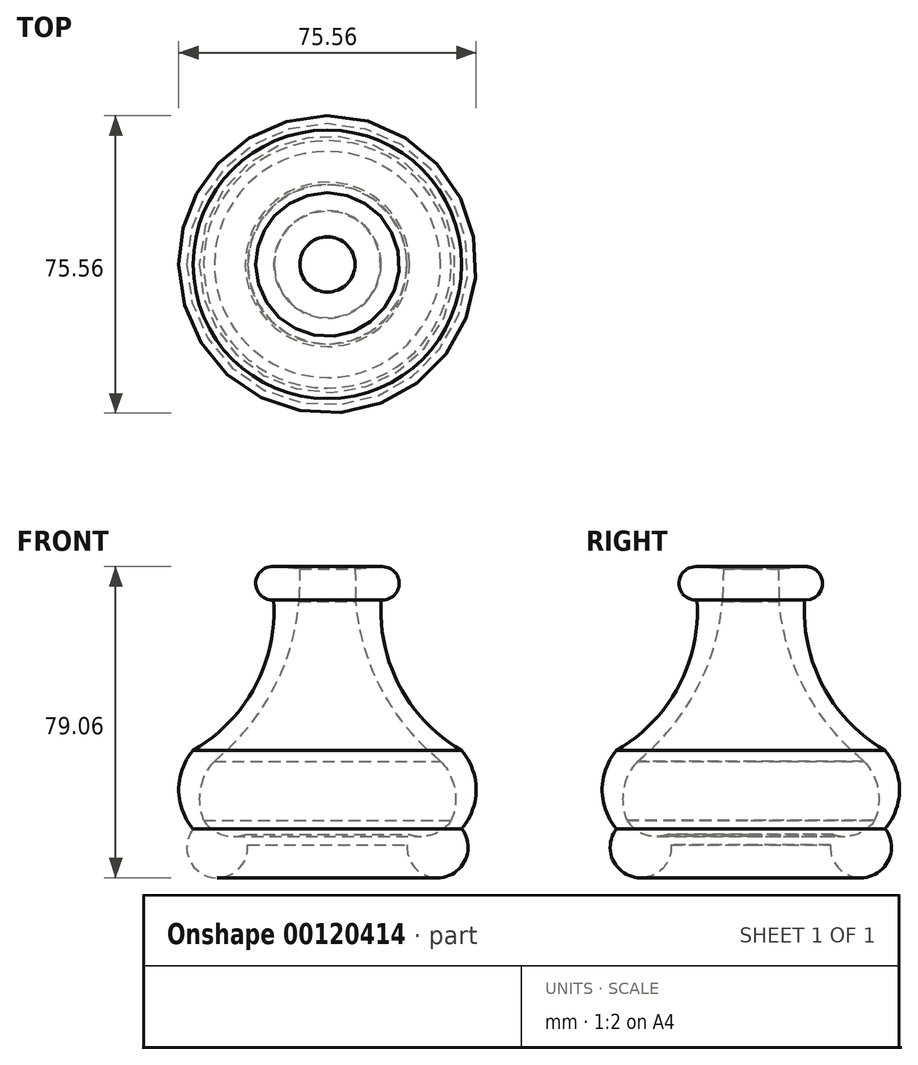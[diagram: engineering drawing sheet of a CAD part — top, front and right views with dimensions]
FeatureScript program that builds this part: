
annotation { "Feature Type Name" : "Feature", "Feature Type Description" : "" }
export const myFeature = defineFeature(function(context is Context, id is Id, definition is map)
    precondition{}
    {
        {
            var Q0;
            Q0=qCreatedBy(makeId("Front.planeOp"),FACE);
            var sketch = newSketch(context, id + "F0", { "sketchPlane" : qUnion([Q0])});
            skLineSegment(sketch, "E0", {"start": v(0, 0) * mm, "end": v(20.26, 0) * mm});
            skArc(sketch, "E1", {"start": v(20.26, 0) * mm, "mid": v(30.2, -8.02) * mm, "end": v(34.11, 4.13) * mm});
            skArc(sketch, "E2", {"start": v(34.11, 4.13) * mm, "mid": v(37.78, 14.06) * mm, "end": v(34.11, 23.98) * mm});
            skArc(sketch, "E3", {"start": v(13.65, 62.23) * mm, "mid": v(18.44, 40.2) * mm, "end": v(34.11, 23.98) * mm});
            skLineSegment(sketch, "E4", {"start": v(13.65, 70.7) * mm, "end": v(7, 70.18) * mm});
            skArc(sketch, "E5", {"start": v(7.22, 61.85) * mm, "mid": v(13.85, 39.38) * mm, "end": v(28.74, 21.29) * mm});
            skArc(sketch, "E6", {"start": v(31.43, 6.2) * mm, "mid": v(32.33, 14.14) * mm, "end": v(28.74, 21.29) * mm});
            skArc(sketch, "E7", {"start": v(20.88, 2.68) * mm, "mid": v(26.75, 2.63) * mm, "end": v(31.43, 6.2) * mm});
            skLineSegment(sketch, "E8", {"start": v(20.88, 2.68) * mm, "end": v(0, 2.68) * mm});
            skLineSegment(sketch, "E9", {"start": v(0, 0) * mm, "end": v(0, 2.68) * mm});
            skArc(sketch, "E10", {"start": v(13.65, 62.23) * mm, "mid": v(18.23, 66.47) * mm, "end": v(13.65, 70.7) * mm});
            skLineSegment(sketch, "E11", {"start": v(7, 70.18) * mm, "end": v(7.22, 61.85) * mm});
            skSolve(sketch);
        }
        {
            var Q0;
            Q0=makeQuery(id+"F0.imprint","IMPRINT",FACE,{"disambiguationData":[TD([[makeQuery(id+"F0.imprint","IMPRINT",EDGE,{"derivedFrom":sQuery(id+"F0.wireOp",EDGE,"E0")}),1.0]])]});
            var Q1;
            Q1=sQuery(id+"F0.wireOp",EDGE,"E9");
            revolve(context, id + "F1", {"entities" : qUnion([Q0]), "axis" : qUnion([Q1]), "revolveType" : RevolveType.FULL});
        }
    });
